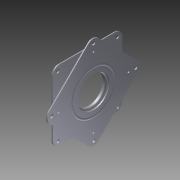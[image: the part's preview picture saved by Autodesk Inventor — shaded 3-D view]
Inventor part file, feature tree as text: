
AUTODESK INVENTOR PART (.ipt)
format: ipt  version: 2014 (Build 180170000, 170)  size: 402,432 bytes
history: native  units: in
note: dims shown in document units (in); Inventor stores cm internally (conversion verified against a paired STEP export)
features: sketch x5, hole x3, revolve x2, plane x2, extrude x2, fillet x2
ambient origin geometry x8: Origin, YZ Plane, XZ Plane, XY Plane, X Axis, Y Axis, Z Axis, Center Point
bodies: Solid1 (feature_tree)
feature tree (16):
  sketch  "Sketch1"  dims[d3=0.0438in d8=0.0438in]
  revolve  "Revolution1"  [1 undecoded]
  revolve  "Revolution2"  [1 undecoded]
  plane  "Work Plane1"
  extrude  "Extrusion1"  Depth=0.001in
  fillet  "Fillet1"  [1 undecoded]
  plane  "Work Plane2"
  extrude  "Extrusion2"  Depth=3.0in
  fillet  "Fillet2"  Radius=3.0in
  sketch  "Sketch4"  dims[d81=90.0deg d82=3.0in d83=3.0in]
  hole  "Hole1"  [1 undecoded]
  hole  "Hole2"  [1 undecoded]
  hole  "Hole3"  [1 undecoded]
  sketch  "Sketch2"  dims[d15=0.0438in d31=0.1565in]
  sketch  "Sketch3"  dims[d39=0.044in d55=0.001in d79=90.0deg]
  sketch  "Sketch5"  dims[d84=0.044in d85=0.0in d86=0.313in d87=3.0in d88=0.1065in d89=0.0in d90=0.313in d91=2.563in d92=0.2185in d93=2.563in d94=2.563in d95=2.563in d96=2.125in d97=0.4375in d98=0.2185in d99=0.4375in d100=2.125in d101=0.4375in d102=0.2185in d103=0.2185in d104=0.4375in d105=0.4375in d106=0.4375in d107=0.156in d108=0.75in d109=0.375in d110=0.25in d111=0.5635in d112=0.156in d113=0.8108in d114=0.094in d115=0.75in d116=0.375in d117=0.25in d118=0.5635in d119=0.156in d120=0.8108in d121=2.563in d122=0.2185in d123=0.2185in d124=0.1783in d125=0.156in d126=0.75in d127=0.375in d128=0.25in d129=0.5635in d130=0.156in d131=0.8108in]
note: 6 required parameter values undecoded (feature->parameter linkage not recoverable at this tier; creation-order binding heuristic only, values carry confidence <= 0.55)